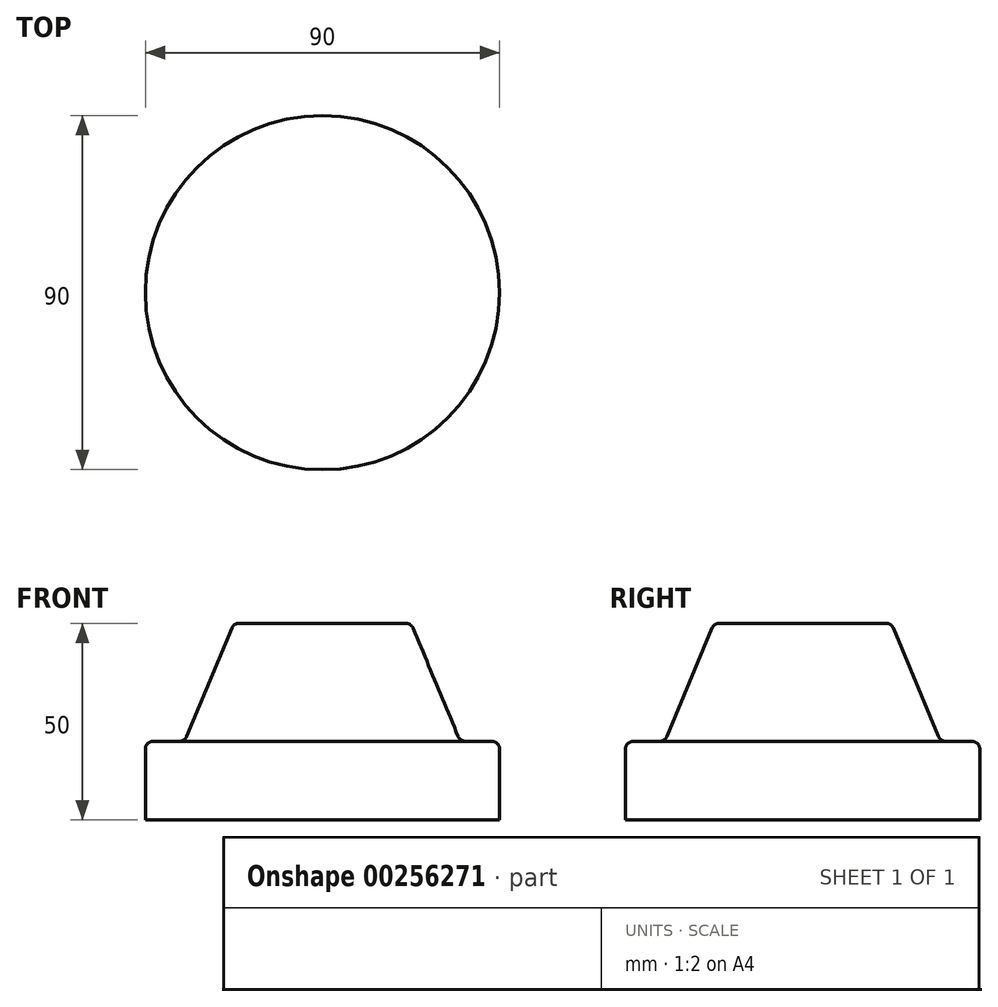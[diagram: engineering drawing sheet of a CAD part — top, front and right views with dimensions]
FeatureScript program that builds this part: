
annotation { "Feature Type Name" : "Feature", "Feature Type Description" : "" }
export const myFeature = defineFeature(function(context is Context, id is Id, definition is map)
    precondition{}
    {
        {
            var Q0;
            Q0=qCreatedBy(makeId("Front.planeOp"),FACE);
            var sketch = newSketch(context, id + "F0", { "sketchPlane" : qUnion([Q0])});
            skLineSegment(sketch, "E0", {"start": v(0, 50) * mm, "end": v(0, 0) * mm});
            skLineSegment(sketch, "E1", {"start": v(0, 0) * mm, "end": v(45, 0) * mm});
            skLineSegment(sketch, "E2", {"start": v(45, 0) * mm, "end": v(45, 18) * mm});
            skLineSegment(sketch, "E3", {"start": v(43, 20) * mm, "end": v(36.33, 20) * mm});
            skLineSegment(sketch, "E4", {"start": v(34.49, 21.23) * mm, "end": v(23.01, 48.77) * mm});
            skLineSegment(sketch, "E5", {"start": v(21.17, 50) * mm, "end": v(0, 50) * mm});
            skPoint(sketch, "E6.visualSharp", {"position": v(22.5, 50) * mm});
            skArc(sketch, "E6.filletArc", {"start": v(23.01, 48.77) * mm, "mid": v(22.28, 49.66) * mm, "end": v(21.17, 50) * mm});
            skPoint(sketch, "E7.visualSharp", {"position": v(35, 20) * mm});
            skArc(sketch, "E7.filletArc", {"start": v(34.49, 21.23) * mm, "mid": v(35.22, 20.34) * mm, "end": v(36.33, 20) * mm});
            skPoint(sketch, "E8.visualSharp", {"position": v(45, 20) * mm});
            skArc(sketch, "E8.filletArc", {"start": v(45, 18) * mm, "mid": v(44.41, 19.41) * mm, "end": v(43, 20) * mm});
            skLineSegment(sketch, "E9", {"start": v(0, 72.15) * mm, "end": v(0, -42.6) * mm});
            skLineSegment(sketch, "E10", {"start": v(0, -33.42) * mm, "end": v(0, 68.14) * mm, "construction": true});
            skSolve(sketch);
        }
        {
            var Q0;
            {var subQ1=sQuery(id+"F0.wireOp",EDGE,"E1");Q0=makeQuery(id+"F0.imprint","IMPRINT",FACE,{"disambiguationData":[TD([[makeQuery(id+"F0.imprint","IMPRINT",EDGE,{"derivedFrom":subQ1}),1.0]])]});}
            var Q1;
            Q1=sQuery(id+"F0.wireOp",EDGE,"E9");
            revolve(context, id + "F1", {"entities" : qUnion([Q0]), "axis" : qUnion([Q1]), "revolveType" : RevolveType.FULL});
        }
    });
